FCSTD DOCUMENT  (FreeCAD 0.21R33694 (Git))
Label: Gun_wall_vertical_mount_holder
License: All rights reserved
objects: Sketcher::SketchObject×1, PartDesign::Body×1
note: 2 computed .brp shape members not serialized (recipe doc carries the construction recipe); baked Part::Feature solids carry a one-line shape summary decoded from their .brp

FEATURE [Sketcher::SketchObject] Sketch
  FullyConstrained = false
  MapMode = 5
  Support = -> [XY_Plane]
  sketch-geometry (8):
    g0: LineSegment StartX=0 StartY=0 StartZ=0 EndX=140 EndY=0 EndZ=0
    g1: LineSegment StartX=140 StartY=-25.7387 StartZ=0 EndX=140 EndY=124.261 EndZ=0
    g2: LineSegment StartX=140 StartY=90 StartZ=0 EndX=0 EndY=90 EndZ=0
    g3: LineSegment StartX=0 StartY=90 StartZ=0 EndX=0 EndY=0 EndZ=0
    g4: LineSegment StartX=40 StartY=50 StartZ=0 EndX=100 EndY=50 EndZ=0
    g5: LineSegment StartX=100 StartY=50 StartZ=0 EndX=100 EndY=20 EndZ=0
    g6: LineSegment StartX=100 StartY=20 StartZ=0 EndX=40 EndY=20 EndZ=0
    g7: LineSegment StartX=40 StartY=20 StartZ=0 EndX=40 EndY=50 EndZ=0
  constraints (1):
    c: DistanceY(g1,g1) = 150
FEATURE [PartDesign::Body] Body
  Group = -> [Sketch]
  Origin = -> Origin
